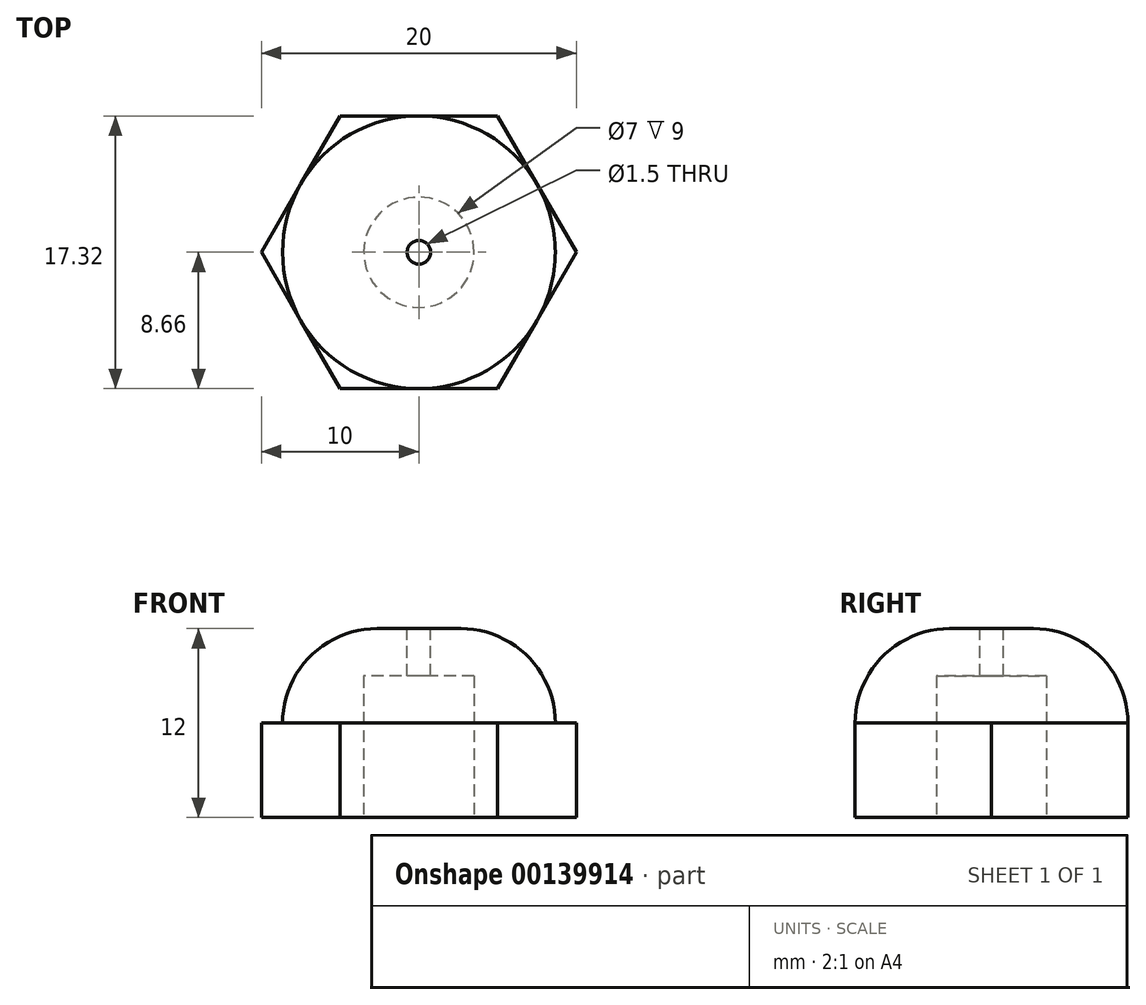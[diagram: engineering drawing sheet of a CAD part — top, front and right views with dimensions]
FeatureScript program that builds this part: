
annotation { "Feature Type Name" : "Feature", "Feature Type Description" : "" }
export const myFeature = defineFeature(function(context is Context, id is Id, definition is map)
    precondition{}
    {
        {
            var Q0;
            Q0=qCreatedBy(makeId("Top.planeOp"),FACE);
            var sketch = newSketch(context, id + "F0", { "sketchPlane" : qUnion([Q0])});
            skCircle(sketch, "E0", {"center": v(0, 0) * mm, "radius": 3.5 * mm});
            skLineSegment(sketch, "E1", {"start": v(-5, 8.66) * mm, "end": v(5, 8.66) * mm});
            skLineSegment(sketch, "E2", {"start": v(-5, 8.66) * mm, "end": v(-10, 0) * mm});
            skLineSegment(sketch, "E3", {"start": v(-10, 0) * mm, "end": v(-5, -8.66) * mm});
            skLineSegment(sketch, "E4", {"start": v(-5, -8.66) * mm, "end": v(5, -8.66) * mm});
            skLineSegment(sketch, "E5", {"start": v(5, -8.66) * mm, "end": v(10, 0) * mm});
            skLineSegment(sketch, "E6", {"start": v(5, 8.66) * mm, "end": v(10, 0) * mm});
            skLineSegment(sketch, "E7", {"start": v(-5, 8.66) * mm, "end": v(5, -8.66) * mm, "construction": true});
            skSolve(sketch);
        }
        {
            var Q0;
            Q0 = qSketchRegion(id + "F0", true);
            extrude(context, id + "F1", {"entities" : qUnion([Q0]), "depth" : 6 * mm});
        }
        {
            var Q0;
            Q0=makeQuery(id+"F1.opExtrude","CAP_FACE",FACE,{"disambiguationData":[OSD([sQuery(id+"F0.wireOp",EDGE,"E0"),sQuery(id+"F0.wireOp",EDGE,"E1"),sQuery(id+"F0.wireOp",EDGE,"E2"),sQuery(id+"F0.wireOp",EDGE,"E3"),sQuery(id+"F0.wireOp",EDGE,"E4"),sQuery(id+"F0.wireOp",EDGE,"E5"),sQuery(id+"F0.wireOp",EDGE,"E6")])],"isStart":false});
            var sketch = newSketch(context, id + "F2", { "sketchPlane" : qUnion([Q0])});
            skCircle(sketch, "E8", {"center": v(0, 0) * mm, "radius": 8.66 * mm});
            skSolve(sketch);
        }
        {
            var Q0;
            Q0 = qSketchRegion(id + "F2", true);
            extrude(context, id + "F3", {"entities" : qUnion([Q0]), "operationType" : NewBodyOperationType.ADD, "depth" : 6 * mm});
        }
        {
            var Q0;
            Q0=makeQuery(id+"F3.opExtrude","CAP_EDGE",EDGE,{"disambiguationData":[OSD([sQuery(id+"F2.wireOp",EDGE,"E8")])],"isStart":false});
            fillet(context, id + "F4", {"entities" : qUnion([Q0]), "radius" : 6 * mm, "tangentPropagation" : true, "allowEdgeOverflow" : false});
        }
        {
            var Q0;
            Q0=makeQuery(id+"F3.opExtrude","CAP_FACE",FACE,{"disambiguationData":[OSD([sQuery(id+"F2.wireOp",EDGE,"E8")])],"isStart":false});
            var sketch = newSketch(context, id + "F5", { "sketchPlane" : qUnion([Q0])});
            skCircle(sketch, "E9", {"center": v(0, 0) * mm, "radius": 0.75 * mm});
            skSolve(sketch);
        }
        {
            var Q0;
            Q0=makeQuery(id+"F3.opExtrude","CAP_FACE",FACE,{"disambiguationData":[OSD([sQuery(id+"F2.wireOp",EDGE,"E8")])],"isStart":true});
            extrude(context, id + "F6", {"entities" : qUnion([Q0]), "operationType" : NewBodyOperationType.REMOVE, "oppositeDirection" : true, "depth" : 3 * mm});
        }
        {
            var Q0;
            Q0 = qSketchRegion(id + "F5", true);
            extrude(context, id + "F7", {"entities" : qUnion([Q0]), "operationType" : NewBodyOperationType.REMOVE, "endBound" : BoundingType.THROUGH_ALL, "oppositeDirection" : true, "depth" : 25 * mm});
        }
    });
